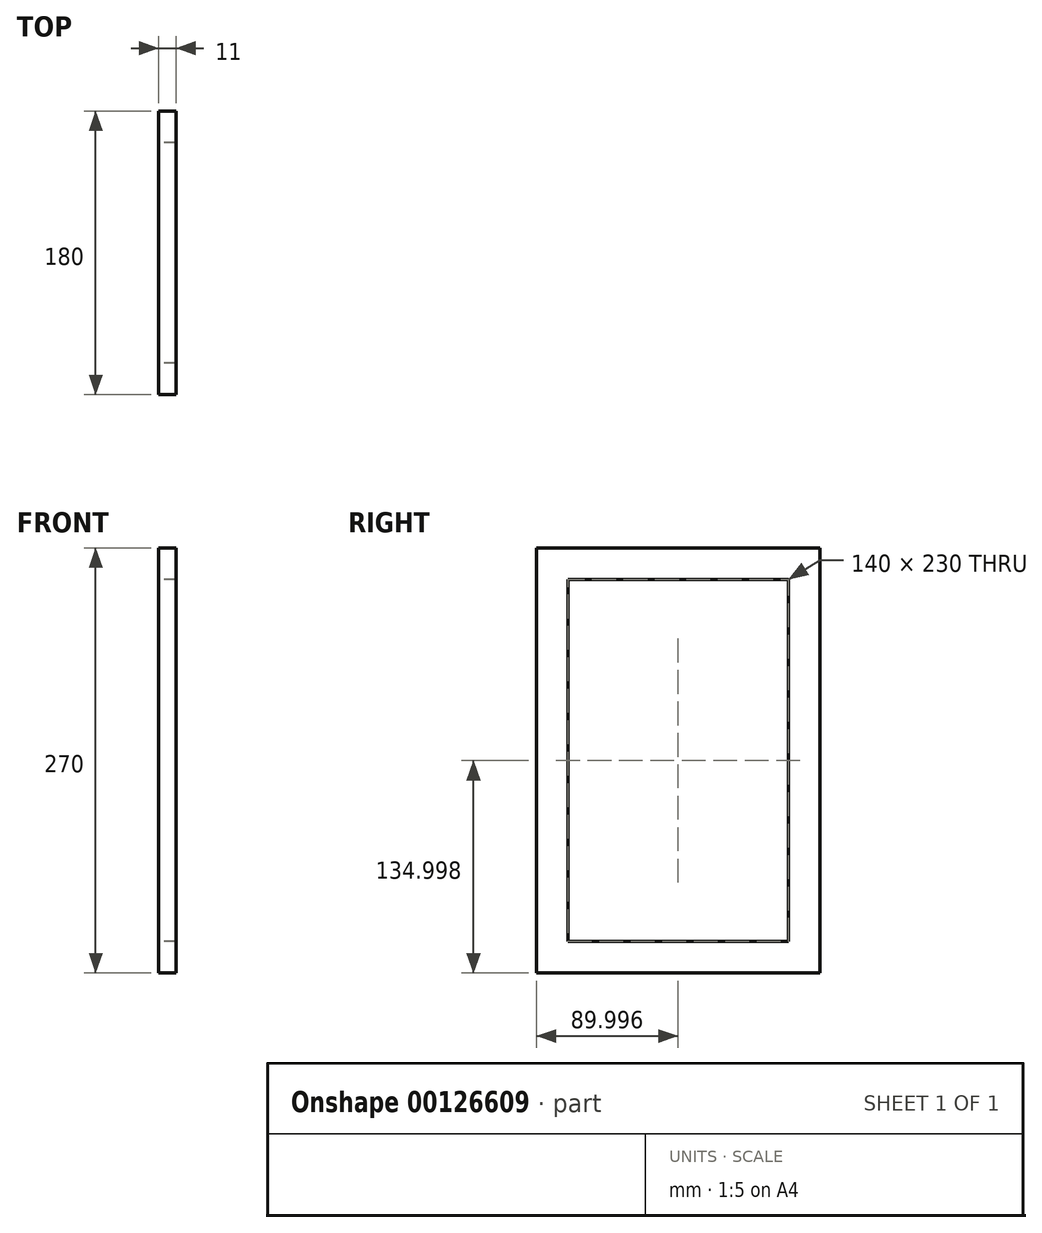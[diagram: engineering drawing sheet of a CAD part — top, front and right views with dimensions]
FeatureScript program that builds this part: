
annotation { "Feature Type Name" : "Feature", "Feature Type Description" : "" }
export const myFeature = defineFeature(function(context is Context, id is Id, definition is map)
    precondition{}
    {
        {
            var Q0;
            Q0=qCreatedBy(makeId("Right.planeOp"),FACE);
            var sketch = newSketch(context, id + "F0", { "sketchPlane" : qUnion([Q0])});
            skLineSegment(sketch, "E0.bottom", {"start": v(-124.16, 132.74) * mm, "end": v(55.84, 132.74) * mm});
            skLineSegment(sketch, "E0.top", {"start": v(-124.16, -137.26) * mm, "end": v(55.84, -137.26) * mm});
            skLineSegment(sketch, "E0.left", {"start": v(-124.16, 132.74) * mm, "end": v(-124.16, -137.26) * mm});
            skLineSegment(sketch, "E0.right", {"start": v(55.84, 132.74) * mm, "end": v(55.84, -137.26) * mm});
            skLineSegment(sketch, "E1.0", {"start": v(-104.16, 112.74) * mm, "end": v(35.84, 112.74) * mm});
            skLineSegment(sketch, "E1.1", {"start": v(-104.16, 112.74) * mm, "end": v(-104.16, -117.26) * mm});
            skLineSegment(sketch, "E1.2", {"start": v(-104.16, -117.26) * mm, "end": v(35.84, -117.26) * mm});
            skLineSegment(sketch, "E1.3", {"start": v(35.84, 112.74) * mm, "end": v(35.84, -117.26) * mm});
            skSolve(sketch);
        }
        {
            var Q0;
            Q0=qSketchRegion(id+"F0",true);
            var Q1;
            Q1=makeQuery(id+"F0.imprint","IMPRINT",FACE,{"disambiguationData":[TD([[makeQuery(id+"F0.imprint","IMPRINT",EDGE,{"derivedFrom":sQuery(id+"F0.wireOp",EDGE,"E0.bottom")}),-1.0]])]});
            extrude(context, id + "F1", {"entities" : qUnion([Q0, Q1]), "depth" : 11 * mm});
        }
    });
